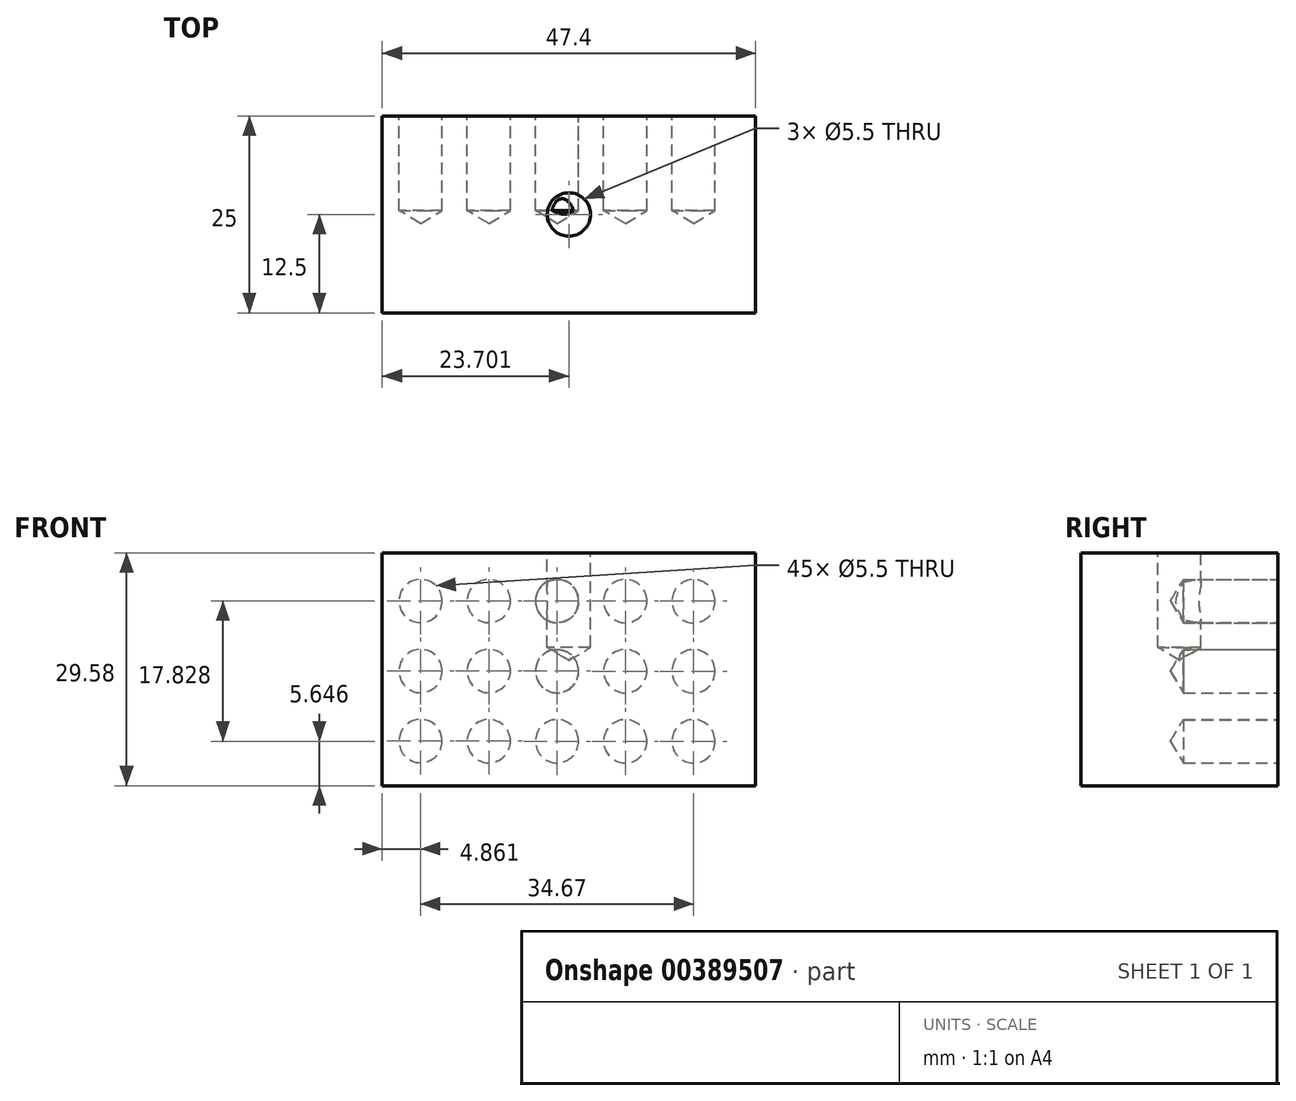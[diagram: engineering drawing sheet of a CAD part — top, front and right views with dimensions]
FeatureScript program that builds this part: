
annotation { "Feature Type Name" : "Feature", "Feature Type Description" : "" }
export const myFeature = defineFeature(function(context is Context, id is Id, definition is map)
    precondition{}
    {
        {
            var Q0;
            Q0=qCreatedBy(makeId("Front.planeOp"),FACE);
            var sketch = newSketch(context, id + "F0", { "sketchPlane" : qUnion([Q0])});
            skLineSegment(sketch, "E0.bottom", {"start": v(0, 0) * mm, "end": v(47.4, 0) * mm});
            skLineSegment(sketch, "E0.top", {"start": v(0, 29.58) * mm, "end": v(47.4, 29.58) * mm});
            skLineSegment(sketch, "E0.left", {"start": v(0, 0) * mm, "end": v(0, 29.58) * mm});
            skLineSegment(sketch, "E0.right", {"start": v(47.4, 0) * mm, "end": v(47.4, 29.58) * mm});
            skSolve(sketch);
        }
        {
            var Q0;
            Q0=makeQuery(id+"F0.imprint","IMPRINT",FACE,{"disambiguationData":[TD([[makeQuery(id+"F0.imprint","IMPRINT",EDGE,{"derivedFrom":sQuery(id+"F0.wireOp",EDGE,"E0.bottom")}),1.0]])]});
            extrude(context, id + "F1", {"entities" : qUnion([Q0]), "depth" : 25 * mm});
        }
        {
            var Q0;
            Q0=makeQuery(id+"F1.opExtrude","SWEPT_FACE",FACE,{"disambiguationData":[OSD([sQuery(id+"F0.wireOp",EDGE,"E0.top")])]});
            var sketch = newSketch(context, id + "F2", { "sketchPlane" : qUnion([Q0])});
            skLineSegment(sketch, "E1", {"start": v(47.4, -25) * mm, "end": v(0, 0) * mm, "construction": true});
            skLineSegment(sketch, "E2", {"start": v(47.4, 0) * mm, "end": v(0, -25) * mm, "construction": true});
            skPoint(sketch, "E3", {"position": v(23.7, -12.5) * mm});
            skSolve(sketch);
        }
        {
            var Q0;
            Q0=sQuery(id+"F2.wireOp",VERTEX,"E3");
            var Q1;
            Q1=makeQuery(id+"F1.opExtrude","SWEPT_BODY",BODY,{"disambiguationData":[OSD([sQuery(id+"F0.wireOp",EDGE,"E0.bottom"),sQuery(id+"F0.wireOp",EDGE,"E0.top"),sQuery(id+"F0.wireOp",EDGE,"E0.left"),sQuery(id+"F0.wireOp",EDGE,"E0.right")])]});
            hole(context, id + "F3", {"style" : HoleStyle.SIMPLE, "endStyle" : HoleEndStyle.BLIND, "standardTappedOrClearance" : lookupTablePath({ "standard" : "ISO", "fit" : "Normal", "size" : "M5", "type" : "Clearance" }), "standardBlindInLast" : lookupTablePath({ "fit" : "Standard", "standard" : "ISO", "size" : "M5", "type" : "Clearance" }), "holeDiameter" : 5.5 * mm, "holeDepth" : 12 * mm, "isTappedThrough" : true, "tappedDepth" : 12 * mm, "tapClearance" : 3, "startFromSketch" : true, "locations" : qUnion([Q0]), "scope" : qUnion([Q1])});
        }
        {
            var Q0;
            Q0=makeQuery(id+"F1.opExtrude","CAP_FACE",FACE,{"disambiguationData":[OSD([sQuery(id+"F0.wireOp",EDGE,"E0.bottom"),sQuery(id+"F0.wireOp",EDGE,"E0.top"),sQuery(id+"F0.wireOp",EDGE,"E0.left"),sQuery(id+"F0.wireOp",EDGE,"E0.right")])],"isStart":true});
            var sketch = newSketch(context, id + "F4", { "sketchPlane" : qUnion([Q0])});
            skPoint(sketch, "E4", {"position": v(-39.53, 23.45) * mm});
            skPoint(sketch, "E5.0.1.0", {"position": v(-39.53, 14.55) * mm});
            skPoint(sketch, "E5.0.2.0", {"position": v(-39.53, 5.65) * mm});
            skPoint(sketch, "E5.1.0.0", {"position": v(-30.86, 23.45) * mm});
            skPoint(sketch, "E5.1.1.0", {"position": v(-30.86, 14.55) * mm});
            skPoint(sketch, "E5.1.2.0", {"position": v(-30.86, 5.65) * mm});
            skPoint(sketch, "E5.2.0.0", {"position": v(-22.2, 23.46) * mm});
            skPoint(sketch, "E5.2.1.0", {"position": v(-22.2, 14.56) * mm});
            skPoint(sketch, "E5.2.2.0", {"position": v(-22.2, 5.66) * mm});
            skPoint(sketch, "E5.3.0.0", {"position": v(-13.53, 23.47) * mm});
            skPoint(sketch, "E5.3.1.0", {"position": v(-13.53, 14.57) * mm});
            skPoint(sketch, "E5.3.2.0", {"position": v(-13.53, 5.67) * mm});
            skPoint(sketch, "E5.4.0.0", {"position": v(-4.86, 23.47) * mm});
            skPoint(sketch, "E5.4.1.0", {"position": v(-4.86, 14.57) * mm});
            skPoint(sketch, "E5.4.2.0", {"position": v(-4.86, 5.67) * mm});
            skLineSegment(sketch, "E5.direction1", {"start": v(-39.53, 23.45) * mm, "end": v(-30.86, 23.45) * mm, "construction": true});
            skLineSegment(sketch, "E5.direction2", {"start": v(-39.53, 23.45) * mm, "end": v(-39.53, 14.55) * mm, "construction": true});
            skSolve(sketch);
        }
        {
            var Q0;
            Q0=sQuery(id+"F4.wireOp",VERTEX,"E4");
            var Q1;
            Q1=sQuery(id+"F4.wireOp",VERTEX,"E5.1.0.0");
            var Q2;
            Q2=sQuery(id+"F4.wireOp",VERTEX,"E5.2.0.0");
            var Q3;
            Q3=sQuery(id+"F4.wireOp",VERTEX,"E5.3.0.0");
            var Q4;
            Q4=sQuery(id+"F4.wireOp",VERTEX,"E5.4.0.0");
            var Q5;
            Q5=sQuery(id+"F4.wireOp",VERTEX,"E5.0.2.0");
            var Q6;
            Q6=sQuery(id+"F4.wireOp",VERTEX,"E5.0.1.0");
            var Q7;
            Q7=sQuery(id+"F4.wireOp",VERTEX,"E5.4.2.0");
            var Q8;
            Q8=sQuery(id+"F4.wireOp",VERTEX,"E5.1.1.0");
            var Q9;
            Q9=sQuery(id+"F4.wireOp",VERTEX,"E5.4.1.0");
            var Q10;
            Q10=sQuery(id+"F4.wireOp",VERTEX,"E5.1.2.0");
            var Q11;
            Q11=sQuery(id+"F4.wireOp",VERTEX,"E5.2.1.0");
            var Q12;
            Q12=sQuery(id+"F4.wireOp",VERTEX,"E5.3.1.0");
            var Q13;
            Q13=sQuery(id+"F4.wireOp",VERTEX,"E5.2.2.0");
            var Q14;
            Q14=sQuery(id+"F4.wireOp",VERTEX,"E5.3.2.0");
            var Q15;
            Q15=makeQuery(id+"F1.opExtrude","SWEPT_BODY",BODY,{"disambiguationData":[OSD([sQuery(id+"F0.wireOp",EDGE,"E0.bottom"),sQuery(id+"F0.wireOp",EDGE,"E0.top"),sQuery(id+"F0.wireOp",EDGE,"E0.left"),sQuery(id+"F0.wireOp",EDGE,"E0.right")])]});
            hole(context, id + "F5", {"style" : HoleStyle.SIMPLE, "endStyle" : HoleEndStyle.BLIND, "standardTappedOrClearance" : lookupTablePath({ "standard" : "ISO", "fit" : "Normal", "size" : "M5", "type" : "Clearance" }), "standardBlindInLast" : lookupTablePath({ "fit" : "Standard", "standard" : "ISO", "size" : "M5", "type" : "Clearance" }), "holeDiameter" : 5.5 * mm, "holeDepth" : 12 * mm, "isTappedThrough" : true, "tappedDepth" : 12 * mm, "tapClearance" : 3, "startFromSketch" : true, "locations" : qUnion([Q0, Q1, Q2, Q3, Q4, Q5, Q6, Q7, Q8, Q9, Q10, Q11, Q12, Q13, Q14]), "scope" : qUnion([Q15])});
        }
    });
